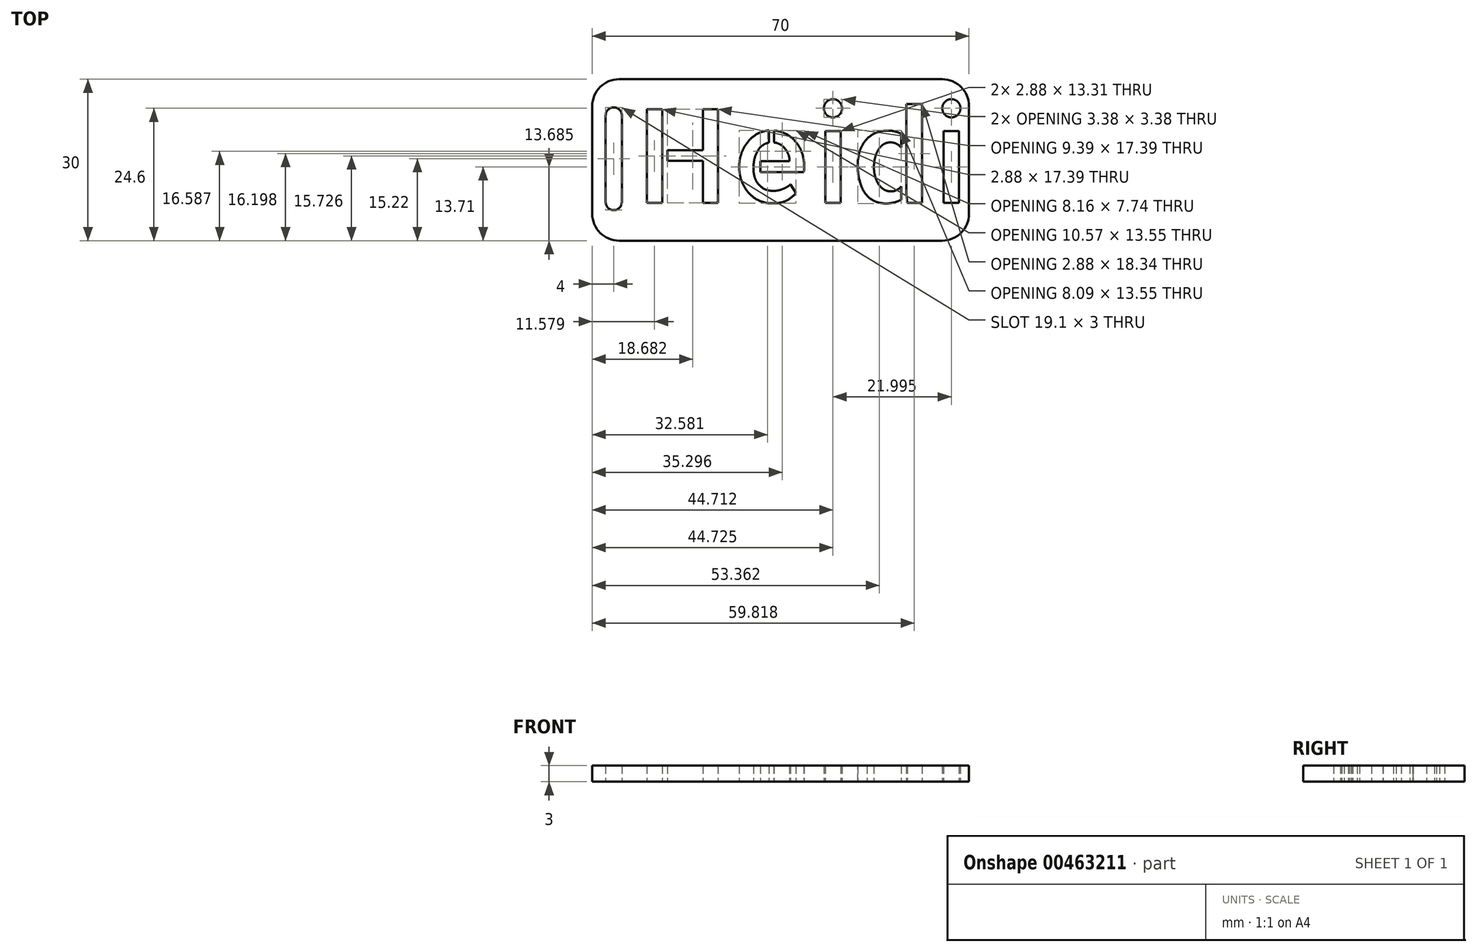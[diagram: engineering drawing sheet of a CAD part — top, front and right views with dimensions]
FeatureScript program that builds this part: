
annotation { "Feature Type Name" : "Feature", "Feature Type Description" : "" }
export const myFeature = defineFeature(function(context is Context, id is Id, definition is map)
    precondition{}
    {
        {
            var Q0;
            Q0=qCreatedBy(makeId("Top.planeOp"),FACE);
            var sketch = newSketch(context, id + "F0", { "sketchPlane" : qUnion([Q0])});
            skLineSegment(sketch, "E0.bottom", {"start": v(35, -15) * mm, "end": v(-35, -15) * mm});
            skLineSegment(sketch, "E0.top", {"start": v(35, 15) * mm, "end": v(-35, 15) * mm});
            skLineSegment(sketch, "E0.left", {"start": v(35, -15) * mm, "end": v(35, 15) * mm});
            skLineSegment(sketch, "E0.right", {"start": v(-35, -15) * mm, "end": v(-35, 15) * mm});
            skPoint(sketch, "E0.middle", {"position": v(0, 0) * mm});
            skPoint(sketch, "E1.endSnap0", {"position": v(-35, 0) * mm});
            skLineSegment(sketch, "E2", {"start": v(-32.5, 0.17) * mm, "end": v(-32.5, 8.27) * mm});
            skLineSegment(sketch, "E3", {"start": v(-29.5, 8.27) * mm, "end": v(-29.5, 0.2) * mm});
            skLineSegment(sketch, "E4", {"start": v(-29.5, 0.2) * mm, "end": v(-29.5, -7.8) * mm});
            skLineSegment(sketch, "E5", {"start": v(-32.5, 0.17) * mm, "end": v(-32.5, -7.83) * mm});
            skArc(sketch, "E6", {"start": v(-29.5, 8.27) * mm, "mid": v(-31, 9.77) * mm, "end": v(-32.5, 8.27) * mm});
            skArc(sketch, "E7", {"start": v(-32.5, -7.83) * mm, "mid": v(-30.99, -9.33) * mm, "end": v(-29.5, -7.8) * mm});
            skLineSegment(sketch, "E8", {"start": v(-27.08, 15) * mm, "end": v(-27.08, -15) * mm});
            skPoint(sketch, "E9.endSnap0", {"position": v(0, -15) * mm});
            skText(sketch, "E10", { "text": "Heidi", "fontName": "AllertaStencil-Regular.ttf"});
            const initialGuessF0  = {"E10": [-0.02708, -0.00797, 1, 0, 0.0174]};
            skSetInitialGuess(sketch, initialGuessF0);
            skSolve(sketch);
        }
        {
            var Q0;
            {var subQ0=sQuery(id+"F0.wireOp",EDGE,"E0.left");Q0=makeQuery(id+"F0.imprint","IMPRINT",FACE,{"disambiguationData":[TD([[makeQuery(id+"F0.imprint","IMPRINT",EDGE,{"derivedFrom":subQ0}),1.0]])]});}
            var Q1;
            {var subQ0=sQuery(id+"F0.wireOp",EDGE,"E0.right");Q1=makeQuery(id+"F0.imprint","IMPRINT",FACE,{"disambiguationData":[TD([[makeQuery(id+"F0.imprint","IMPRINT",EDGE,{"derivedFrom":subQ0}),-1.0]])]});}
            extrude(context, id + "F1", {"entities" : qUnion([Q0, Q1]), "depth" : 3 * mm});
        }
        {
            var Q0;
            Q0=makeQuery(id+"F1.opExtrude","SWEPT_EDGE",EDGE,{"disambiguationData":[OSD([sQuery(id+"F0.wireOp",EDGE,"E0.bottom"),sQuery(id+"F0.wireOp",EDGE,"E0.right")])]});
            var Q1;
            Q1=makeQuery(id+"F1.opExtrude","SWEPT_EDGE",EDGE,{"disambiguationData":[OSD([sQuery(id+"F0.wireOp",EDGE,"E0.top"),sQuery(id+"F0.wireOp",EDGE,"E0.right")])]});
            var Q2;
            Q2=makeQuery(id+"F1.opExtrude","SWEPT_EDGE",EDGE,{"disambiguationData":[OSD([sQuery(id+"F0.wireOp",EDGE,"E0.bottom"),sQuery(id+"F0.wireOp",EDGE,"E0.left")])]});
            var Q3;
            Q3=makeQuery(id+"F1.opExtrude","SWEPT_EDGE",EDGE,{"disambiguationData":[OSD([sQuery(id+"F0.wireOp",EDGE,"E0.top"),sQuery(id+"F0.wireOp",EDGE,"E0.left")])]});
            fillet(context, id + "F2", {"entities" : qUnion([Q0, Q1, Q2, Q3]), "radius" : 5 * mm, "tangentPropagation" : true, "allowEdgeOverflow" : false});
        }
    });
